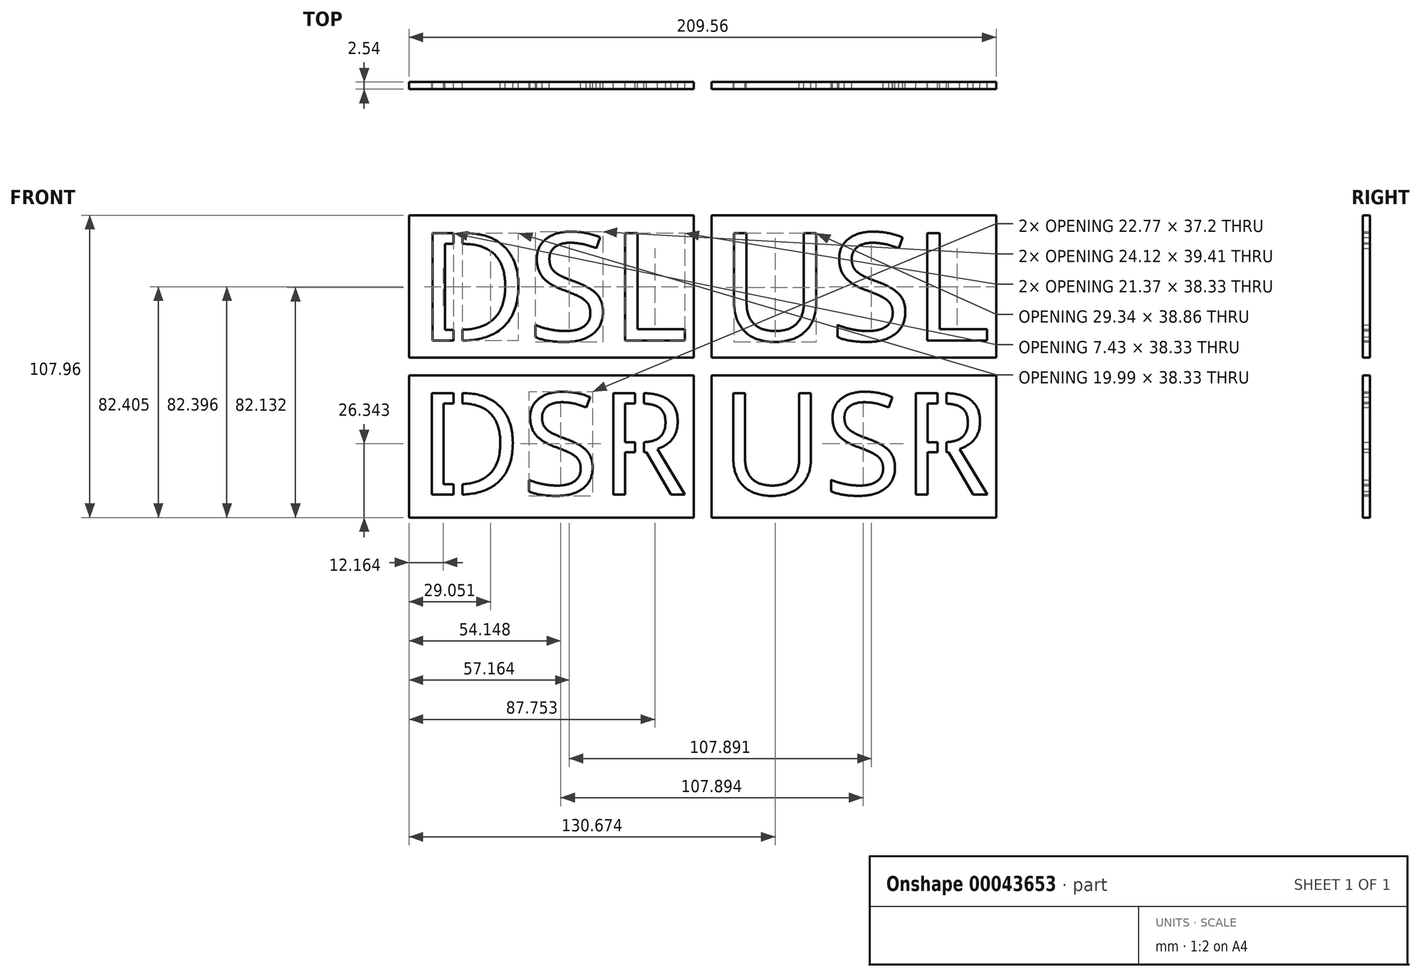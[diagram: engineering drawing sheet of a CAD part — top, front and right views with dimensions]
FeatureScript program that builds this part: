
annotation { "Feature Type Name" : "Feature", "Feature Type Description" : "" }
export const myFeature = defineFeature(function(context is Context, id is Id, definition is map)
    precondition{}
    {
        {
            var Q0;
            Q0=qCreatedBy(makeId("Front.planeOp"),FACE);
            var sketch = newSketch(context, id + "F0", { "sketchPlane" : qUnion([Q0])});
            skLineSegment(sketch, "E0.bottom", {"start": v(-104.78, 3.17) * mm, "end": v(-3.18, 3.17) * mm});
            skLineSegment(sketch, "E0.top", {"start": v(-104.78, 53.97) * mm, "end": v(-3.18, 53.97) * mm});
            skLineSegment(sketch, "E0.left", {"start": v(-104.78, 3.17) * mm, "end": v(-104.78, 53.97) * mm});
            skLineSegment(sketch, "E0.right", {"start": v(-3.18, 3.17) * mm, "end": v(-3.18, 53.97) * mm});
            skLineSegment(sketch, "E1.bottom", {"start": v(3.17, 3.17) * mm, "end": v(104.77, 3.18) * mm});
            skLineSegment(sketch, "E1.top", {"start": v(3.17, 53.97) * mm, "end": v(104.77, 53.98) * mm});
            skLineSegment(sketch, "E1.left", {"start": v(3.17, 3.17) * mm, "end": v(3.17, 53.97) * mm});
            skLineSegment(sketch, "E1.right", {"start": v(104.77, 3.18) * mm, "end": v(104.77, 53.98) * mm});
            skLineSegment(sketch, "E2.bottom", {"start": v(104.78, -3.17) * mm, "end": v(3.17, -3.17) * mm});
            skLineSegment(sketch, "E2.top", {"start": v(104.78, -53.97) * mm, "end": v(3.17, -53.98) * mm});
            skLineSegment(sketch, "E2.left", {"start": v(104.77, -3.17) * mm, "end": v(104.78, -53.97) * mm});
            skLineSegment(sketch, "E2.right", {"start": v(3.17, -3.17) * mm, "end": v(3.17, -53.97) * mm});
            skLineSegment(sketch, "E3.bottom", {"start": v(-3.18, -3.18) * mm, "end": v(-104.78, -3.18) * mm});
            skLineSegment(sketch, "E3.top", {"start": v(-3.17, -53.98) * mm, "end": v(-104.78, -53.98) * mm});
            skLineSegment(sketch, "E3.left", {"start": v(-3.18, -3.18) * mm, "end": v(-3.17, -53.98) * mm});
            skLineSegment(sketch, "E3.right", {"start": v(-104.78, -3.18) * mm, "end": v(-104.78, -53.98) * mm});
            skLineSegment(sketch, "E4", {"start": v(-3.17, -3.17) * mm, "end": v(3.18, 3.18) * mm, "construction": true});
            skLineSegment(sketch, "E5", {"start": v(3.18, -3.17) * mm, "end": v(-3.18, 3.17) * mm, "construction": true});
            skLineSegment(sketch, "E6", {"start": v(-3.18, 3.17) * mm, "end": v(-3.18, -3.18) * mm, "construction": true});
            skLineSegment(sketch, "E7", {"start": v(3.17, -3.17) * mm, "end": v(3.17, 3.17) * mm, "construction": true});
            skLineSegment(sketch, "E8", {"start": v(-3.18, 3.17) * mm, "end": v(3.17, 3.17) * mm, "construction": true});
            skLineSegment(sketch, "E9", {"start": v(3.17, -3.17) * mm, "end": v(-3.18, -3.17) * mm, "construction": true});
            skText(sketch, "E10", { "text": "DSL", "fontName": "OpenSans-Regular.ttf"});
            skLineSegment(sketch, "E11", {"start": v(-53.98, 53.97) * mm, "end": v(-53.98, 47.9) * mm, "construction": true});
            skLineSegment(sketch, "E12", {"start": v(-3.18, 28.57) * mm, "end": v(-6.35, 28.57) * mm, "construction": true});
            skLineSegment(sketch, "E13", {"start": v(-101.6, 28.57) * mm, "end": v(-104.78, 28.57) * mm, "construction": true});
            skText(sketch, "E14", { "text": "USL", "fontName": "OpenSans-Regular.ttf"});
            skText(sketch, "E15", { "text": "DSR", "fontName": "OpenSans-Regular.ttf"});
            skText(sketch, "E16", { "text": "USR", "fontName": "OpenSans-Regular.ttf"});
            skLineSegment(sketch, "E17", {"start": v(3.17, 28.57) * mm, "end": v(6.35, 28.57) * mm, "construction": true});
            skLineSegment(sketch, "E18", {"start": v(-53.98, -3.18) * mm, "end": v(-53.98, -9.25) * mm, "construction": true});
            skLineSegment(sketch, "E19", {"start": v(-85.73, -50.8) * mm, "end": v(-85.73, 50.8) * mm});
            skLineSegment(sketch, "E20", {"start": v(-85.73, 50.8) * mm, "end": v(-88.9, 50.8) * mm});
            skLineSegment(sketch, "E21", {"start": v(-88.9, 50.8) * mm, "end": v(-88.9, -50.8) * mm});
            skLineSegment(sketch, "E22", {"start": v(-88.9, -50.8) * mm, "end": v(-85.73, -50.8) * mm});
            skLineSegment(sketch, "E23.bottom", {"start": v(-24.13, -6.35) * mm, "end": v(-20.95, -6.35) * mm});
            skLineSegment(sketch, "E23.top", {"start": v(-24.13, -31.75) * mm, "end": v(-20.95, -31.75) * mm});
            skLineSegment(sketch, "E23.left", {"start": v(-24.13, -6.35) * mm, "end": v(-24.13, -31.75) * mm});
            skLineSegment(sketch, "E23.right", {"start": v(-20.96, -6.35) * mm, "end": v(-20.95, -31.75) * mm});
            skLineSegment(sketch, "E24.bottom", {"start": v(83.82, -6.35) * mm, "end": v(87, -6.35) * mm});
            skLineSegment(sketch, "E24.top", {"start": v(83.82, -31.75) * mm, "end": v(87, -31.75) * mm});
            skLineSegment(sketch, "E24.left", {"start": v(83.82, -6.35) * mm, "end": v(83.82, -31.75) * mm});
            skLineSegment(sketch, "E24.right", {"start": v(87, -6.35) * mm, "end": v(87, -31.75) * mm});
            skLineSegment(sketch, "E25", {"start": v(-20.95, -19.05) * mm, "end": v(-3.17, -19.05) * mm, "construction": true});
            skLineSegment(sketch, "E26", {"start": v(87, -19.05) * mm, "end": v(104.78, -19.05) * mm, "construction": true});
            const initialGuessF0  = {"E10": [-0.1016, 0.00925, 1, 0, 0.03866], "E14": [0.00635, 0.00925, 1, 0, 0.03866], "E15": [-0.1016, -0.04574, 1, 0, 0.0365], "E16": [0.00635, -0.04574, 1, 0, 0.0365]};
            skSetInitialGuess(sketch, initialGuessF0);
            skSolve(sketch);
        }
        {
            var Q0;
            Q0=makeQuery(id+"F0.imprint","IMPRINT",FACE,{"disambiguationData":[TD([[makeQuery(id+"F0.imprint","IMPRINT",EDGE,{"derivedFrom":sQuery(id+"F0.wireOp",EDGE,"E0.top")}),-1.0]])]});
            var Q1;
            Q1=makeQuery(id+"F0.imprint","IMPRINT",FACE,{"disambiguationData":[TD([[makeQuery(id+"F0.imprint","IMPRINT",EDGE,{"derivedFrom":sQuery(id+"F0.wireOp",EDGE,"E10.sketch_text.stroke-7")}),1.0]])]});
            var Q2;
            {var subQ0=sQuery(id+"F0.wireOp",EDGE,"E19");var subQ1=sQuery(id+"F0.wireOp",EDGE,"E10.sketch_text.stroke-9");var subQ2=makeQuery(id+"F0.imprint","INTERSECT",VERTEX,{"derivedFrom":[subQ1,subQ0]});Q2=makeQuery(id+"F0.imprint","IMPRINT",FACE,{"disambiguationData":[TD([[makeQuery(id+"F0.imprint","IMPRINT",EDGE,{"disambiguationData":[TD([[subQ2,-1.0]])],"derivedFrom":subQ1}),1.0]])]});}
            var Q3;
            {var subQ0=sQuery(id+"F0.wireOp",EDGE,"E10.sketch_text.stroke-10");Q3=makeQuery(id+"F0.imprint","IMPRINT",FACE,{"disambiguationData":[TD([[makeQuery(id+"F0.imprint","IMPRINT",EDGE,{"derivedFrom":subQ0}),1.0]])]});}
            var Q4;
            {var subQ0=sQuery(id+"F0.wireOp",EDGE,"E21");var subQ1=sQuery(id+"F0.wireOp",EDGE,"E10.sketch_text.stroke-4");var subQ2=makeQuery(id+"F0.imprint","INTERSECT",VERTEX,{"derivedFrom":[subQ1,subQ0]});Q4=makeQuery(id+"F0.imprint","IMPRINT",FACE,{"disambiguationData":[TD([[makeQuery(id+"F0.imprint","IMPRINT",EDGE,{"disambiguationData":[TD([[subQ2,-1.0]])],"derivedFrom":subQ1}),-1.0]])]});}
            var Q5;
            {var subQ5=sQuery(id+"F0.wireOp",EDGE,"E20");Q5=makeQuery(id+"F0.imprint","IMPRINT",FACE,{"disambiguationData":[TD([[makeQuery(id+"F0.imprint","IMPRINT",EDGE,{"derivedFrom":subQ5}),1.0]])]});}
            var Q6;
            {var subQ0=sQuery(id+"F0.wireOp",EDGE,"E19");var subQ1=sQuery(id+"F0.wireOp",EDGE,"E10.sketch_text.stroke-2");var subQ2=makeQuery(id+"F0.imprint","INTERSECT",VERTEX,{"derivedFrom":[subQ1,subQ0]});Q6=makeQuery(id+"F0.imprint","IMPRINT",FACE,{"disambiguationData":[TD([[makeQuery(id+"F0.imprint","IMPRINT",EDGE,{"disambiguationData":[TD([[subQ2,-1.0]])],"derivedFrom":subQ1}),-1.0]])]});}
            var Q7;
            {var subQ0=sQuery(id+"F0.wireOp",EDGE,"E21");var subQ1=sQuery(id+"F0.wireOp",EDGE,"E0.bottom");var subQ2=makeQuery(id+"F0.imprint","INTERSECT",VERTEX,{"derivedFrom":[subQ1,subQ0]});Q7=makeQuery(id+"F0.imprint","IMPRINT",FACE,{"disambiguationData":[TD([[makeQuery(id+"F0.imprint","IMPRINT",EDGE,{"disambiguationData":[TD([[subQ2,-1.0]])],"derivedFrom":subQ1}),1.0]])]});}
            var Q8;
            Q8=makeQuery(id+"F0.imprint","IMPRINT",FACE,{"disambiguationData":[TD([[makeQuery(id+"F0.imprint","IMPRINT",EDGE,{"derivedFrom":sQuery(id+"F0.wireOp",EDGE,"E1.bottom")}),1.0]])]});
            var Q9;
            Q9=makeQuery(id+"F0.imprint","IMPRINT",FACE,{"disambiguationData":[TD([[makeQuery(id+"F0.imprint","IMPRINT",EDGE,{"derivedFrom":sQuery(id+"F0.wireOp",EDGE,"E3.top")}),-1.0]])]});
            var Q10;
            {var subQ0=sQuery(id+"F0.wireOp",EDGE,"E19");var subQ1=sQuery(id+"F0.wireOp",EDGE,"E3.bottom");var subQ2=makeQuery(id+"F0.imprint","INTERSECT",VERTEX,{"derivedFrom":[subQ1,subQ0]});Q10=makeQuery(id+"F0.imprint","IMPRINT",FACE,{"disambiguationData":[TD([[makeQuery(id+"F0.imprint","IMPRINT",EDGE,{"disambiguationData":[TD([[subQ2,-1.0]])],"derivedFrom":subQ1}),1.0]])]});}
            var Q11;
            {var subQ1=sQuery(id+"F0.wireOp",EDGE,"E15.sketch_text.stroke-4");var subQ7=sQuery(id+"F0.wireOp",EDGE,"E21");var subQ9=makeQuery(id+"F0.imprint","INTERSECT",VERTEX,{"derivedFrom":[subQ1,subQ7]});Q11=makeQuery(id+"F0.imprint","IMPRINT",FACE,{"disambiguationData":[TD([[makeQuery(id+"F0.imprint","IMPRINT",EDGE,{"disambiguationData":[TD([[subQ9,-1.0]])],"derivedFrom":subQ1}),-1.0]])]});}
            var Q12;
            {var subQ7=sQuery(id+"F0.wireOp",EDGE,"E15.sketch_text.stroke-9");var subQ8=sQuery(id+"F0.wireOp",EDGE,"E15.sketch_text.stroke-8");var subQ9=makeQuery(id+"F0.imprint","INTERSECT",VERTEX,{"derivedFrom":[subQ8,subQ7]});Q12=makeQuery(id+"F0.imprint","IMPRINT",FACE,{"disambiguationData":[TD([[makeQuery(id+"F0.imprint","IMPRINT",EDGE,{"disambiguationData":[TD([[subQ9,1.0]])],"derivedFrom":subQ8}),1.0]])]});}
            var Q13;
            {var subQ0=sQuery(id+"F0.wireOp",EDGE,"E15.sketch_text.stroke-10");Q13=makeQuery(id+"F0.imprint","IMPRINT",FACE,{"disambiguationData":[TD([[makeQuery(id+"F0.imprint","IMPRINT",EDGE,{"derivedFrom":subQ0}),1.0]])]});}
            var Q14;
            {var subQ5=sQuery(id+"F0.wireOp",EDGE,"E15.sketch_text.stroke-7");Q14=makeQuery(id+"F0.imprint","IMPRINT",FACE,{"disambiguationData":[TD([[makeQuery(id+"F0.imprint","IMPRINT",EDGE,{"derivedFrom":subQ5}),1.0]])]});}
            var Q15;
            {var subQ7=sQuery(id+"F0.wireOp",EDGE,"E15.sketch_text.stroke-2");var subQ8=sQuery(id+"F0.wireOp",EDGE,"E15.sketch_text.stroke-1");var subQ9=makeQuery(id+"F0.imprint","INTERSECT",VERTEX,{"derivedFrom":[subQ8,subQ7]});Q15=makeQuery(id+"F0.imprint","IMPRINT",FACE,{"disambiguationData":[TD([[makeQuery(id+"F0.imprint","IMPRINT",EDGE,{"disambiguationData":[TD([[subQ9,1.0]])],"derivedFrom":subQ8}),-1.0]])]});}
            var Q16;
            {var subQ0=sQuery(id+"F0.wireOp",EDGE,"E22");Q16=makeQuery(id+"F0.imprint","IMPRINT",FACE,{"disambiguationData":[TD([[makeQuery(id+"F0.imprint","IMPRINT",EDGE,{"derivedFrom":subQ0}),1.0]])]});}
            var Q17;
            {var subQ5=sQuery(id+"F0.wireOp",EDGE,"E15.sketch_text.stroke-51");var subQ6=sQuery(id+"F0.wireOp",EDGE,"E15.sketch_text.stroke-50");var subQ7=makeQuery(id+"F0.imprint","INTERSECT",VERTEX,{"derivedFrom":[subQ6,subQ5]});Q17=makeQuery(id+"F0.imprint","IMPRINT",FACE,{"disambiguationData":[TD([[makeQuery(id+"F0.imprint","IMPRINT",EDGE,{"disambiguationData":[TD([[subQ7,1.0]])],"derivedFrom":subQ6}),1.0]])]});}
            var Q18;
            {var subQ7=sQuery(id+"F0.wireOp",EDGE,"E15.sketch_text.stroke-43");var subQ8=sQuery(id+"F0.wireOp",EDGE,"E15.sketch_text.stroke-42");var subQ9=makeQuery(id+"F0.imprint","INTERSECT",VERTEX,{"derivedFrom":[subQ8,subQ7]});Q18=makeQuery(id+"F0.imprint","IMPRINT",FACE,{"disambiguationData":[TD([[makeQuery(id+"F0.imprint","IMPRINT",EDGE,{"disambiguationData":[TD([[subQ9,1.0]])],"derivedFrom":subQ8}),-1.0]])]});}
            var Q19;
            {var subQ6=sQuery(id+"F0.wireOp",EDGE,"E23.bottom");Q19=makeQuery(id+"F0.imprint","IMPRINT",FACE,{"disambiguationData":[TD([[makeQuery(id+"F0.imprint","IMPRINT",EDGE,{"derivedFrom":subQ6}),-1.0]])]});}
            var Q20;
            {var subQ1=sQuery(id+"F0.wireOp",EDGE,"E15.sketch_text.stroke-49");var subQ5=sQuery(id+"F0.wireOp",EDGE,"E23.right");var subQ6=makeQuery(id+"F0.imprint","INTERSECT",VERTEX,{"derivedFrom":[subQ1,subQ5]});Q20=makeQuery(id+"F0.imprint","IMPRINT",FACE,{"disambiguationData":[TD([[makeQuery(id+"F0.imprint","IMPRINT",EDGE,{"disambiguationData":[TD([[subQ6,-1.0]])],"derivedFrom":subQ1}),-1.0]])]});}
            var Q21;
            {var subQ0=sQuery(id+"F0.wireOp",EDGE,"E15.sketch_text.stroke-56");Q21=makeQuery(id+"F0.imprint","IMPRINT",FACE,{"disambiguationData":[TD([[makeQuery(id+"F0.imprint","IMPRINT",EDGE,{"derivedFrom":subQ0}),1.0]])]});}
            var Q22;
            {var subQ4=sQuery(id+"F0.wireOp",EDGE,"E15.sketch_text.stroke-52");Q22=makeQuery(id+"F0.imprint","IMPRINT",FACE,{"disambiguationData":[TD([[makeQuery(id+"F0.imprint","IMPRINT",EDGE,{"derivedFrom":subQ4}),1.0]])]});}
            var Q23;
            {var subQ5=sQuery(id+"F0.wireOp",EDGE,"E23.top");Q23=makeQuery(id+"F0.imprint","IMPRINT",FACE,{"disambiguationData":[TD([[makeQuery(id+"F0.imprint","IMPRINT",EDGE,{"derivedFrom":subQ5}),1.0]])]});}
            var Q24;
            Q24=makeQuery(id+"F0.imprint","IMPRINT",FACE,{"disambiguationData":[TD([[makeQuery(id+"F0.imprint","IMPRINT",EDGE,{"derivedFrom":sQuery(id+"F0.wireOp",EDGE,"E2.bottom")}),1.0]])]});
            var Q25;
            {var subQ5=sQuery(id+"F0.wireOp",EDGE,"E24.top");Q25=makeQuery(id+"F0.imprint","IMPRINT",FACE,{"disambiguationData":[TD([[makeQuery(id+"F0.imprint","IMPRINT",EDGE,{"derivedFrom":subQ5}),1.0]])]});}
            var Q26;
            {var subQ1=sQuery(id+"F0.wireOp",EDGE,"E16.sketch_text.stroke-49");var subQ7=sQuery(id+"F0.wireOp",EDGE,"E24.right");var subQ9=makeQuery(id+"F0.imprint","INTERSECT",VERTEX,{"derivedFrom":[subQ1,subQ7]});Q26=makeQuery(id+"F0.imprint","IMPRINT",FACE,{"disambiguationData":[TD([[makeQuery(id+"F0.imprint","IMPRINT",EDGE,{"disambiguationData":[TD([[subQ9,-1.0]])],"derivedFrom":subQ1}),-1.0]])]});}
            var Q27;
            {var subQ5=sQuery(id+"F0.wireOp",EDGE,"E16.sketch_text.stroke-51");var subQ6=sQuery(id+"F0.wireOp",EDGE,"E16.sketch_text.stroke-50");var subQ7=makeQuery(id+"F0.imprint","INTERSECT",VERTEX,{"derivedFrom":[subQ6,subQ5]});Q27=makeQuery(id+"F0.imprint","IMPRINT",FACE,{"disambiguationData":[TD([[makeQuery(id+"F0.imprint","IMPRINT",EDGE,{"disambiguationData":[TD([[subQ7,1.0]])],"derivedFrom":subQ6}),1.0]])]});}
            var Q28;
            {var subQ7=sQuery(id+"F0.wireOp",EDGE,"E16.sketch_text.stroke-43");var subQ8=sQuery(id+"F0.wireOp",EDGE,"E16.sketch_text.stroke-42");var subQ9=makeQuery(id+"F0.imprint","INTERSECT",VERTEX,{"derivedFrom":[subQ8,subQ7]});Q28=makeQuery(id+"F0.imprint","IMPRINT",FACE,{"disambiguationData":[TD([[makeQuery(id+"F0.imprint","IMPRINT",EDGE,{"disambiguationData":[TD([[subQ9,1.0]])],"derivedFrom":subQ8}),-1.0]])]});}
            var Q29;
            {var subQ1=sQuery(id+"F0.wireOp",EDGE,"E24.bottom");Q29=makeQuery(id+"F0.imprint","IMPRINT",FACE,{"disambiguationData":[TD([[makeQuery(id+"F0.imprint","IMPRINT",EDGE,{"derivedFrom":subQ1}),-1.0]])]});}
            var Q30;
            {var subQ0=sQuery(id+"F0.wireOp",EDGE,"E16.sketch_text.stroke-56");Q30=makeQuery(id+"F0.imprint","IMPRINT",FACE,{"disambiguationData":[TD([[makeQuery(id+"F0.imprint","IMPRINT",EDGE,{"derivedFrom":subQ0}),1.0]])]});}
            var Q31;
            {var subQ6=sQuery(id+"F0.wireOp",EDGE,"E16.sketch_text.stroke-52");Q31=makeQuery(id+"F0.imprint","IMPRINT",FACE,{"disambiguationData":[TD([[makeQuery(id+"F0.imprint","IMPRINT",EDGE,{"derivedFrom":subQ6}),1.0]])]});}
            extrude(context, id + "F1", {"entities" : qUnion([Q0, Q1, Q2, Q3, Q4, Q5, Q6, Q7, Q8, Q9, Q10, Q11, Q12, Q13, Q14, Q15, Q16, Q17, Q18, Q19, Q20, Q21, Q22, Q23, Q24, Q25, Q26, Q27, Q28, Q29, Q30, Q31]), "depth" : 2.54 * mm});
        }
    });
